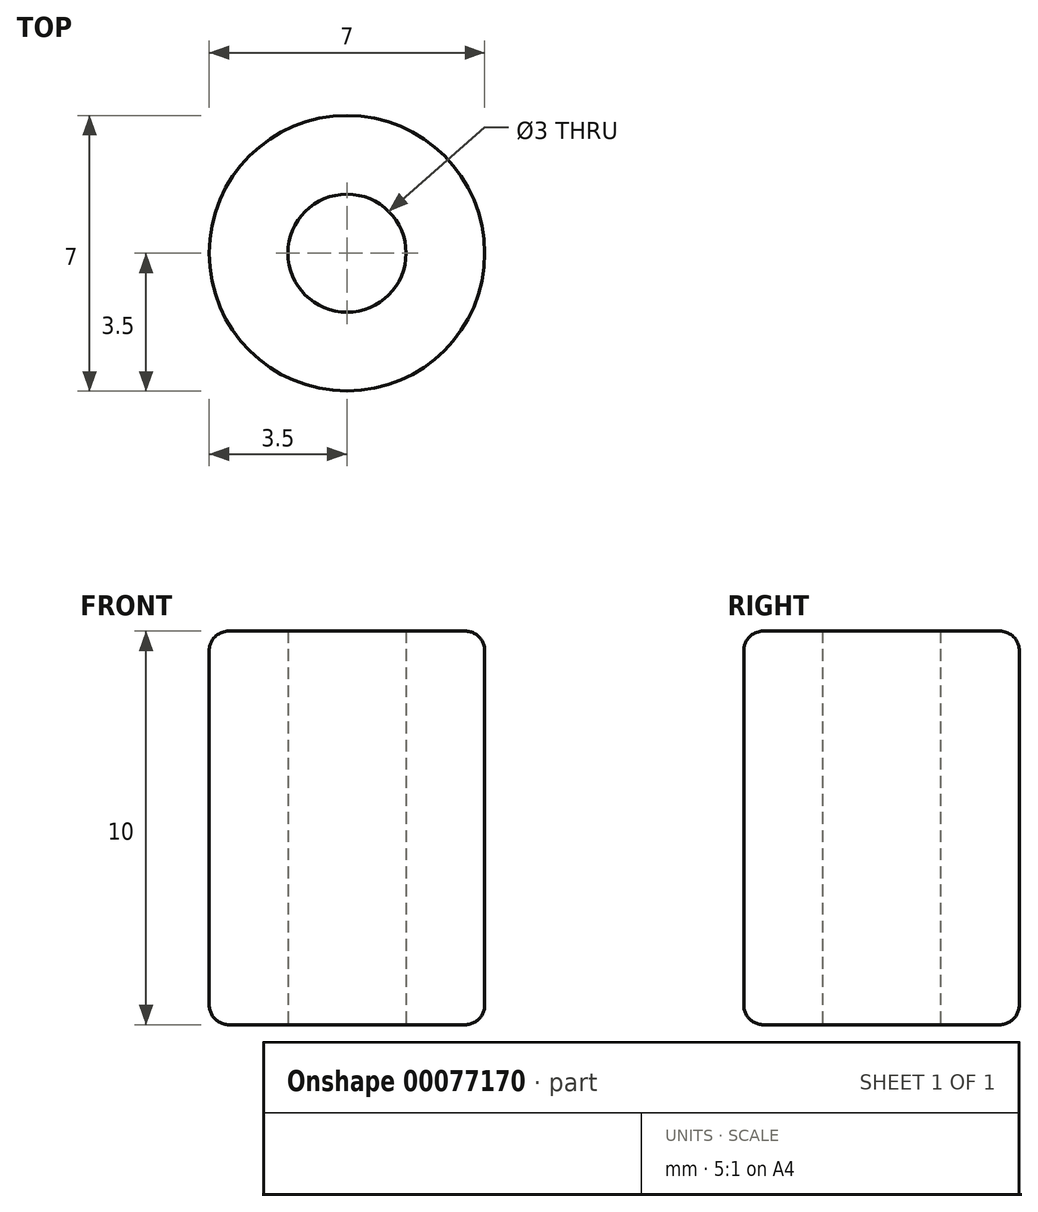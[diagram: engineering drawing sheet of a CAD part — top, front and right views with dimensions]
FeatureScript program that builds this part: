
annotation { "Feature Type Name" : "Feature", "Feature Type Description" : "" }
export const myFeature = defineFeature(function(context is Context, id is Id, definition is map)
    precondition{}
    {
        {
            var Q0;
            Q0=qCreatedBy(makeId("Top.planeOp"),FACE);
            var sketch = newSketch(context, id + "F0", { "sketchPlane" : qUnion([Q0])});
            skCircle(sketch, "E0", {"center": v(0, 0) * mm, "radius": 3.5 * mm});
            skCircle(sketch, "E1", {"center": v(0, 0) * mm, "radius": 1.5 * mm});
            skSolve(sketch);
        }
        {
            var Q0;
            Q0=qSketchRegion(id+"F0",true);
            extrude(context, id + "F1", {"entities" : qUnion([Q0]), "depth" : 10 * mm});
        }
        {
            var Q0;
            Q0=makeQuery(id+"F1.opExtrude","CAP_EDGE",EDGE,{"disambiguationData":[OSD([sQuery(id+"F0.wireOp",EDGE,"E0")])],"isStart":false});
            var Q1;
            Q1=makeQuery(id+"F1.opExtrude","CAP_EDGE",EDGE,{"disambiguationData":[OSD([sQuery(id+"F0.wireOp",EDGE,"E0")])],"isStart":true});
            fillet(context, id + "F2", {"entities" : qUnion([Q0, Q1]), "radius" : .5 * mm, "tangentPropagation" : true, "allowEdgeOverflow" : false});
        }
    });
